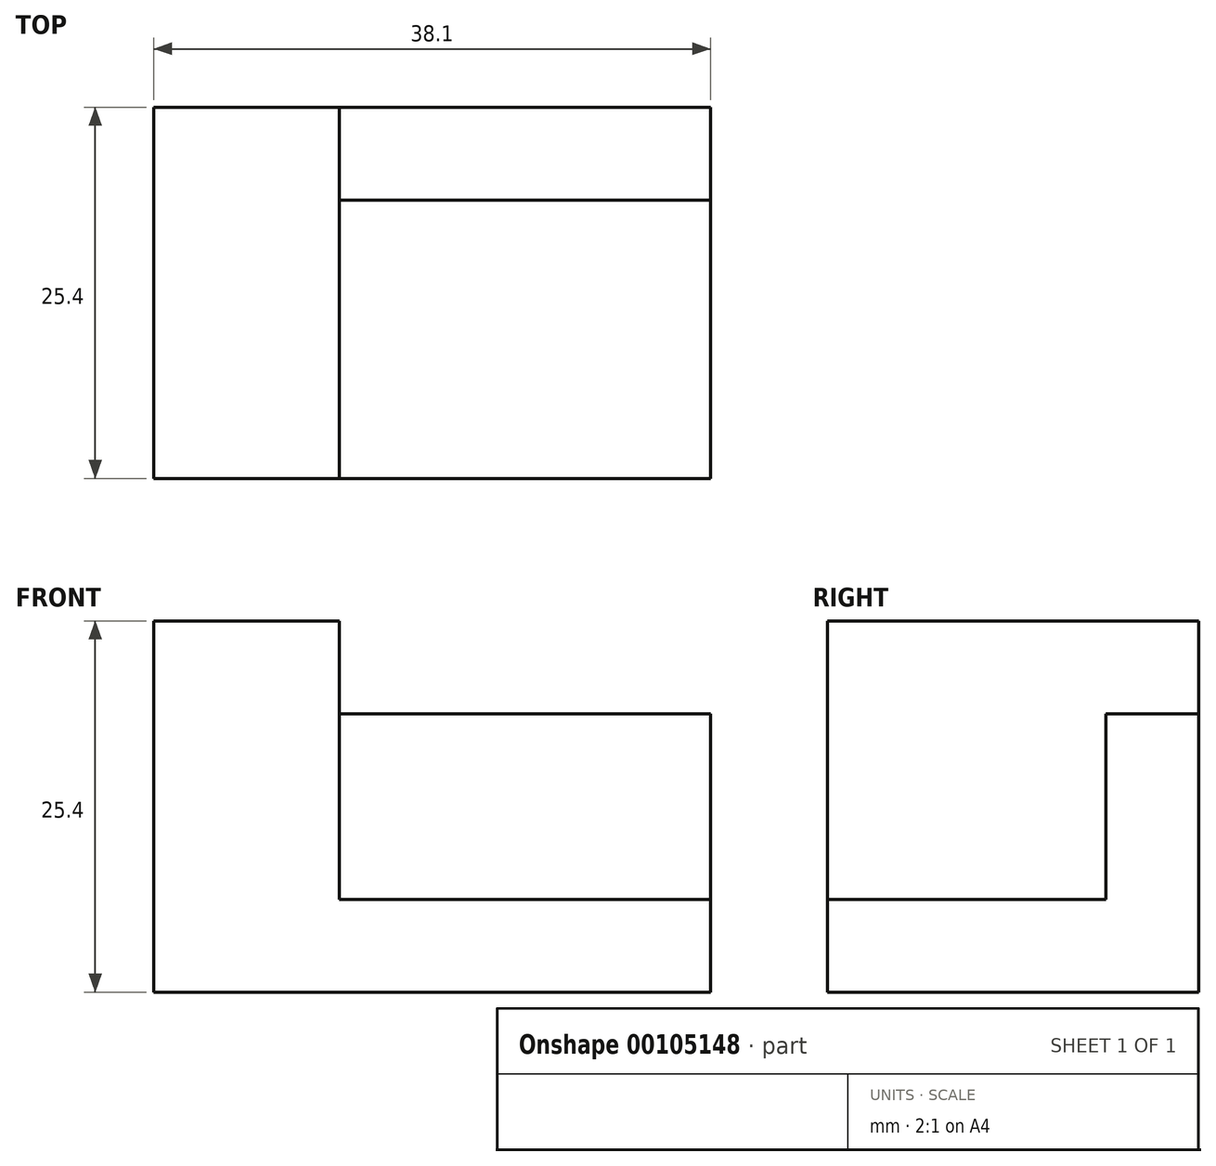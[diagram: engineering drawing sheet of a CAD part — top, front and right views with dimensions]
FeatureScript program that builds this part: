
annotation { "Feature Type Name" : "Feature", "Feature Type Description" : "" }
export const myFeature = defineFeature(function(context is Context, id is Id, definition is map)
    precondition{}
    {
        {
            var Q0;
            Q0=qCreatedBy(makeId("Front.planeOp"),FACE);
            var sketch = newSketch(context, id + "F0", { "sketchPlane" : qUnion([Q0])});
            skLineSegment(sketch, "E0.bottom", {"start": v(0, 0) * mm, "end": v(38.1, 0) * mm});
            skLineSegment(sketch, "E0.top", {"start": v(0, 25.4) * mm, "end": v(38.1, 25.4) * mm});
            skLineSegment(sketch, "E0.left", {"start": v(0, 0) * mm, "end": v(0, 25.4) * mm});
            skLineSegment(sketch, "E0.right", {"start": v(38.1, 0) * mm, "end": v(38.1, 25.4) * mm});
            skSolve(sketch);
        }
        {
            var Q0;
            Q0 = qSketchRegion(id + "F0", true);
            extrude(context, id + "F1", {"entities" : qUnion([Q0]), "depth" : 25.4 * mm});
        }
        {
            var Q0;
            Q0=makeQuery(id+"F1.opExtrude","CAP_FACE",FACE,{"disambiguationData":[OSD([sQuery(id+"F0.wireOp",EDGE,"E0.bottom"),sQuery(id+"F0.wireOp",EDGE,"E0.top"),sQuery(id+"F0.wireOp",EDGE,"E0.left"),sQuery(id+"F0.wireOp",EDGE,"E0.right")])],"isStart":false});
            var sketch = newSketch(context, id + "F2", { "sketchPlane" : qUnion([Q0])});
            skLineSegment(sketch, "E1.bottom", {"start": v(12.7, 25.4) * mm, "end": v(38.1, 25.4) * mm});
            skLineSegment(sketch, "E1.top", {"start": v(12.7, 6.35) * mm, "end": v(38.1, 6.35) * mm});
            skLineSegment(sketch, "E1.left", {"start": v(12.7, 25.4) * mm, "end": v(12.7, 6.35) * mm});
            skLineSegment(sketch, "E1.right", {"start": v(38.1, 25.4) * mm, "end": v(38.1, 6.35) * mm});
            skSolve(sketch);
        }
        {
            var Q0;
            Q0 = qSketchRegion(id + "F2", true);
            extrude(context, id + "F3", {"entities" : qUnion([Q0]), "operationType" : NewBodyOperationType.REMOVE, "oppositeDirection" : true, "depth" : 19.05 * mm});
        }
        {
            var Q0;
            Q0=makeQuery(id+"F1.opExtrude","SWEPT_FACE",FACE,{"disambiguationData":[OSD([sQuery(id+"F0.wireOp",EDGE,"E0.right")])]});
            var sketch = newSketch(context, id + "F4", { "sketchPlane" : qUnion([Q0])});
            skLineSegment(sketch, "E2.bottom", {"start": v(-6.35, 25.4) * mm, "end": v(0, 25.4) * mm});
            skLineSegment(sketch, "E2.top", {"start": v(-6.35, 19.05) * mm, "end": v(0, 19.05) * mm});
            skLineSegment(sketch, "E2.left", {"start": v(-6.35, 25.4) * mm, "end": v(-6.35, 19.05) * mm});
            skLineSegment(sketch, "E2.right", {"start": v(0, 25.4) * mm, "end": v(0, 19.05) * mm});
            skSolve(sketch);
        }
        {
            var Q0;
            Q0 = qSketchRegion(id + "F4", true);
            extrude(context, id + "F5", {"entities" : qUnion([Q0]), "operationType" : NewBodyOperationType.REMOVE, "oppositeDirection" : true, "depth" : 25.4 * mm});
        }
    });
